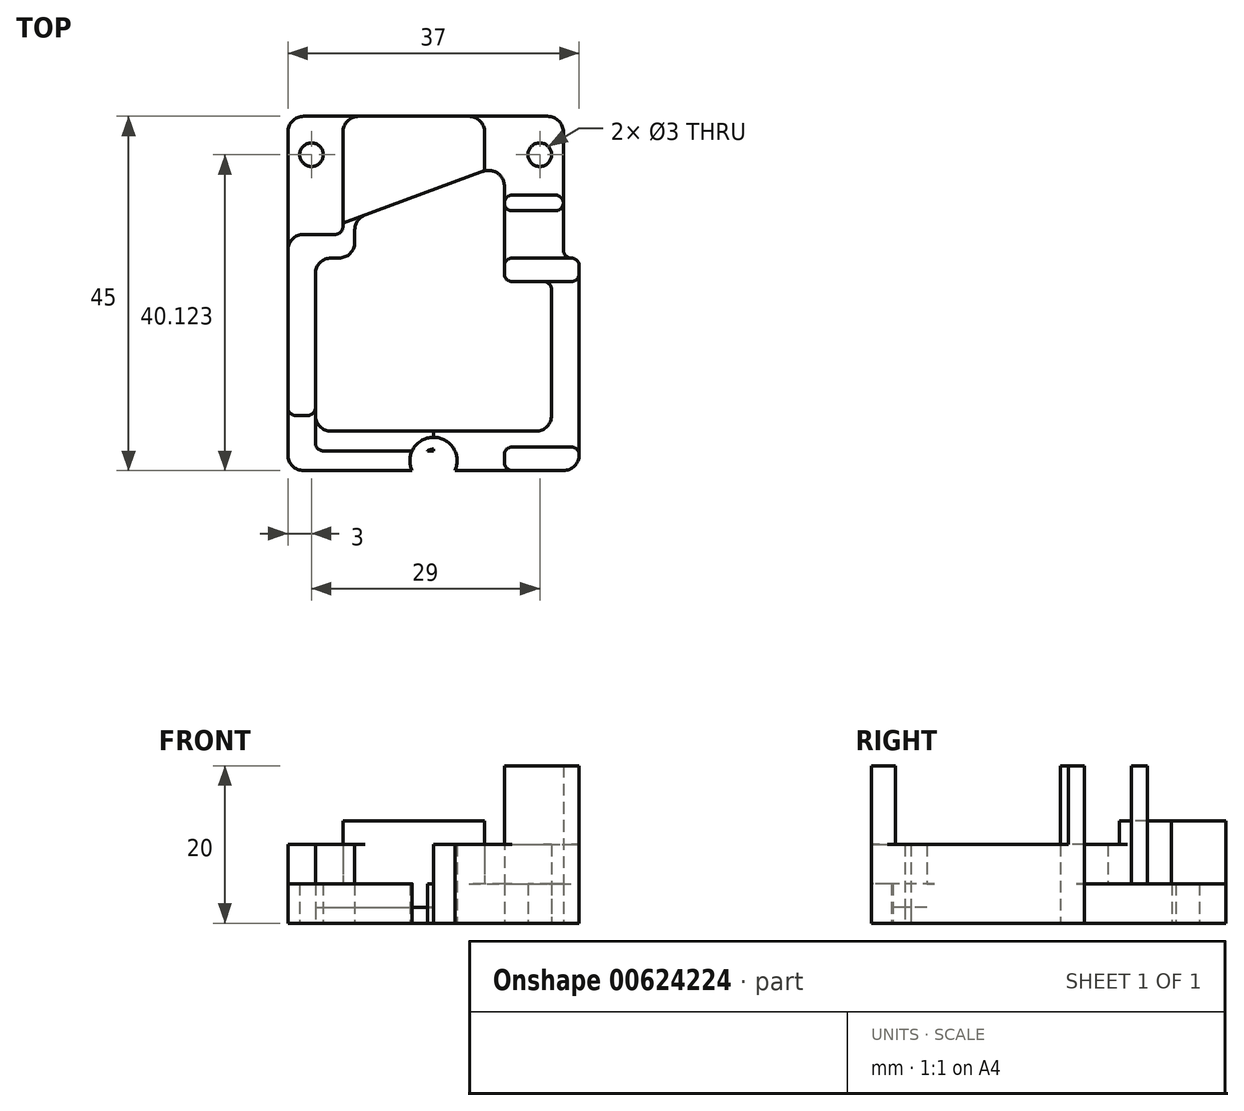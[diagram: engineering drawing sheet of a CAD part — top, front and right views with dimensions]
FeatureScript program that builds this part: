
annotation { "Feature Type Name" : "Feature", "Feature Type Description" : "" }
export const myFeature = defineFeature(function(context is Context, id is Id, definition is map)
    precondition{}
    {
        {
            var Q0;
            Q0=qCreatedBy(makeId("Top.planeOp"),FACE);
            var sketch = newSketch(context, id + "F0", { "sketchPlane" : qUnion([Q0])});
            skLineSegment(sketch, "E0.bottom", {"start": v(-16.5, 22.5) * mm, "end": v(14.5, 22.5) * mm});
            skLineSegment(sketch, "E0.top", {"start": v(-16.5, -22.5) * mm, "end": v(16.5, -22.5) * mm});
            skLineSegment(sketch, "E0.left", {"start": v(-18.5, 20.5) * mm, "end": v(-18.5, -20.5) * mm});
            skLineSegment(sketch, "E0.right", {"start": v(18.5, 3.5) * mm, "end": v(18.5, -20.5) * mm});
            skPoint(sketch, "E0.middle", {"position": v(0, 0) * mm});
            skLineSegment(sketch, "E1", {"start": v(-15, 2.5) * mm, "end": v(-15, -15.5) * mm});
            skLineSegment(sketch, "E2", {"start": v(-13, -17.5) * mm, "end": v(13, -17.5) * mm});
            skLineSegment(sketch, "E3", {"start": v(15, -15.5) * mm, "end": v(15, 0.5) * mm});
            skLineSegment(sketch, "E4", {"start": v(-13, 4.5) * mm, "end": v(-12, 4.5) * mm});
            skLineSegment(sketch, "E5", {"start": v(-10, 6.5) * mm, "end": v(-10, 8.1) * mm});
            skLineSegment(sketch, "E6", {"start": v(10, 1.5) * mm, "end": v(14, 1.5) * mm});
            skLineSegment(sketch, "E7", {"start": v(9, 2.5) * mm, "end": v(9, 13.63) * mm});
            skLineSegment(sketch, "E8", {"start": v(6.3, 15.5) * mm, "end": v(-8.7, 9.98) * mm});
            skLineSegment(sketch, "E9", {"start": v(16.5, 20.5) * mm, "end": v(16.5, 5.5) * mm});
            skLineSegment(sketch, "E10", {"start": v(17.5, 4.5) * mm, "end": v(17.5, 4.5) * mm});
            skPoint(sketch, "E11.visualSharp", {"position": v(-15, -17.5) * mm});
            skArc(sketch, "E11.filletArc", {"start": v(-15, -15.5) * mm, "mid": v(-14.41, -16.91) * mm, "end": v(-13, -17.5) * mm});
            skPoint(sketch, "E12.visualSharp", {"position": v(15, -17.5) * mm});
            skArc(sketch, "E12.filletArc", {"start": v(13, -17.5) * mm, "mid": v(14.41, -16.91) * mm, "end": v(15, -15.5) * mm});
            skPoint(sketch, "E13.visualSharp", {"position": v(-10, 4.5) * mm});
            skArc(sketch, "E13.filletArc", {"start": v(-12, 4.5) * mm, "mid": v(-10.59, 5.09) * mm, "end": v(-10, 6.5) * mm});
            skPoint(sketch, "E14.visualSharp", {"position": v(9, 16.5) * mm});
            skArc(sketch, "E14.filletArc", {"start": v(9, 13.63) * mm, "mid": v(8.14, 15.27) * mm, "end": v(6.3, 15.5) * mm});
            skPoint(sketch, "E15.visualSharp", {"position": v(-15, 4.5) * mm});
            skArc(sketch, "E15.filletArc", {"start": v(-13, 4.5) * mm, "mid": v(-14.41, 3.91) * mm, "end": v(-15, 2.5) * mm});
            skPoint(sketch, "E16.visualSharp", {"position": v(-10, 9.5) * mm});
            skArc(sketch, "E16.filletArc", {"start": v(-8.7, 9.98) * mm, "mid": v(-9.64, 9.25) * mm, "end": v(-10, 8.1) * mm});
            skPoint(sketch, "E17.visualSharp", {"position": v(-18.5, 22.5) * mm});
            skArc(sketch, "E17.filletArc", {"start": v(-16.5, 22.5) * mm, "mid": v(-17.91, 21.91) * mm, "end": v(-18.5, 20.5) * mm});
            skPoint(sketch, "E18.visualSharp", {"position": v(16.5, 22.5) * mm});
            skArc(sketch, "E18.filletArc", {"start": v(16.5, 20.5) * mm, "mid": v(15.91, 21.91) * mm, "end": v(14.5, 22.5) * mm});
            skPoint(sketch, "E19.visualSharp", {"position": v(18.5, -22.5) * mm});
            skArc(sketch, "E19.filletArc", {"start": v(16.5, -22.5) * mm, "mid": v(17.91, -21.91) * mm, "end": v(18.5, -20.5) * mm});
            skPoint(sketch, "E20.visualSharp", {"position": v(-18.5, -22.5) * mm});
            skArc(sketch, "E20.filletArc", {"start": v(-18.5, -20.5) * mm, "mid": v(-17.91, -21.91) * mm, "end": v(-16.5, -22.5) * mm});
            skPoint(sketch, "E21.visualSharp", {"position": v(9, 1.5) * mm});
            skArc(sketch, "E21.filletArc", {"start": v(9, 2.5) * mm, "mid": v(9.3, 1.8) * mm, "end": v(10, 1.5) * mm});
            skPoint(sketch, "E22.visualSharp", {"position": v(15, 1.5) * mm});
            skArc(sketch, "E22.filletArc", {"start": v(15, 0.5) * mm, "mid": v(14.7, 1.2) * mm, "end": v(14, 1.5) * mm});
            skPoint(sketch, "E23.visualSharp", {"position": v(16.5, 4.5) * mm});
            skArc(sketch, "E23.filletArc", {"start": v(16.5, 5.5) * mm, "mid": v(16.8, 4.8) * mm, "end": v(17.5, 4.5) * mm});
            skPoint(sketch, "E24.visualSharp", {"position": v(18.5, 4.5) * mm});
            skArc(sketch, "E24.filletArc", {"start": v(18.5, 3.5) * mm, "mid": v(18.2, 4.2) * mm, "end": v(17.5, 4.5) * mm});
            skLineSegment(sketch, "E25", {"start": v(-14, -20) * mm, "end": v(14, -20) * mm});
            skLineSegment(sketch, "E26", {"start": v(-15, -15.5) * mm, "end": v(-15, -19) * mm});
            skLineSegment(sketch, "E27", {"start": v(15, -15.5) * mm, "end": v(15, -19) * mm});
            skPoint(sketch, "E28.visualSharp", {"position": v(-15, -20) * mm});
            skArc(sketch, "E28.filletArc", {"start": v(-15, -19) * mm, "mid": v(-14.7, -19.7) * mm, "end": v(-14, -20) * mm});
            skPoint(sketch, "E29.visualSharp", {"position": v(15, -20) * mm});
            skArc(sketch, "E29.filletArc", {"start": v(14, -20) * mm, "mid": v(14.7, -19.7) * mm, "end": v(15, -19) * mm});
            skLineSegment(sketch, "E30", {"start": v(0, -17.5) * mm, "end": v(0, -23.8) * mm});
            skPoint(sketch, "E30.endSnap0", {"position": v(0, -22.5) * mm});
            skCircle(sketch, "E31", {"center": v(0, -21.28) * mm, "radius": 3 * mm});
            skCircle(sketch, "E32", {"center": v(0, -21.28) * mm, "radius": 1.5 * mm});
            skCircle(sketch, "E33", {"center": v(-15.5, 17.62) * mm, "radius": 3 * mm});
            skCircle(sketch, "E34", {"center": v(-15.5, 17.62) * mm, "radius": 1.5 * mm});
            skLineSegment(sketch, "E35", {"start": v(-15.5, 17.62) * mm, "end": v(14.6, 17.62) * mm, "construction": true});
            skCircle(sketch, "E36", {"center": v(13.5, 17.62) * mm, "radius": 3 * mm});
            skCircle(sketch, "E37", {"center": v(13.5, 17.62) * mm, "radius": 1.5 * mm});
            skSolve(sketch);
        }
        {
            var Q0;
            Q0=makeQuery(id+"F0.imprint","IMPRINT",FACE,{"disambiguationData":[TD([[makeQuery(id+"F0.imprint","IMPRINT",EDGE,{"derivedFrom":sQuery(id+"F0.wireOp",EDGE,"E0.bottom")}),-1.0]])]});
            var Q1;
            {var subQ0=sQuery(id+"F0.wireOp",EDGE,"E32");var subQ1=sQuery(id+"F0.wireOp",EDGE,"E25");var subQ2=makeQuery(id+"F0.imprint","INTERSECT",VERTEX,{"disambiguationData":[OD(1.0)],"derivedFrom":[subQ1,subQ0]});Q1=makeQuery(id+"F0.imprint","IMPRINT",FACE,{"disambiguationData":[TD([[makeQuery(id+"F0.imprint","IMPRINT",EDGE,{"disambiguationData":[TD([[subQ2,-1.0]])],"derivedFrom":subQ1}),1.0]])]});}
            var Q2;
            {var subQ0=sQuery(id+"F0.wireOp",EDGE,"E31");var subQ1=sQuery(id+"F0.wireOp",EDGE,"E25");var subQ2=makeQuery(id+"F0.imprint","INTERSECT",VERTEX,{"disambiguationData":[OD(0.0)],"derivedFrom":[subQ1,subQ0]});Q2=makeQuery(id+"F0.imprint","IMPRINT",FACE,{"disambiguationData":[TD([[makeQuery(id+"F0.imprint","IMPRINT",EDGE,{"disambiguationData":[TD([[subQ2,-1.0]])],"derivedFrom":subQ1}),1.0]])]});}
            var Q3;
            {var subQ0=sQuery(id+"F0.wireOp",EDGE,"E31");var subQ1=sQuery(id+"F0.wireOp",EDGE,"E0.top");var subQ2=makeQuery(id+"F0.imprint","INTERSECT",VERTEX,{"disambiguationData":[OD(1.0)],"derivedFrom":[subQ1,subQ0]});Q3=makeQuery(id+"F0.imprint","IMPRINT",FACE,{"disambiguationData":[TD([[makeQuery(id+"F0.imprint","IMPRINT",EDGE,{"disambiguationData":[TD([[subQ2,1.0]])],"derivedFrom":subQ1}),1.0]])]});}
            var Q4;
            {var subQ0=sQuery(id+"F0.wireOp",EDGE,"E31");var subQ1=sQuery(id+"F0.wireOp",EDGE,"E0.top");var subQ2=makeQuery(id+"F0.imprint","INTERSECT",VERTEX,{"disambiguationData":[OD(0.0)],"derivedFrom":[subQ1,subQ0]});Q4=makeQuery(id+"F0.imprint","IMPRINT",FACE,{"disambiguationData":[TD([[makeQuery(id+"F0.imprint","IMPRINT",EDGE,{"disambiguationData":[TD([[subQ2,-1.0]])],"derivedFrom":subQ1}),1.0]])]});}
            var Q5;
            {var subQ2=sQuery(id+"F0.wireOp",EDGE,"E0.top");var subQ4=sQuery(id+"F0.wireOp",EDGE,"E31");var subQ5=makeQuery(id+"F0.imprint","INTERSECT",VERTEX,{"disambiguationData":[OD(0.0)],"derivedFrom":[subQ2,subQ4]});Q5=makeQuery(id+"F0.imprint","IMPRINT",FACE,{"disambiguationData":[TD([[makeQuery(id+"F0.imprint","IMPRINT",EDGE,{"disambiguationData":[TD([[subQ5,-1.0]])],"derivedFrom":subQ2}),-1.0]])]});}
            var Q6;
            Q6=makeQuery(id+"F0.imprint","IMPRINT",FACE,{"disambiguationData":[TD([[makeQuery(id+"F0.imprint","IMPRINT",EDGE,{"derivedFrom":sQuery(id+"F0.wireOp",EDGE,"E33")}),1.0]])]});
            var Q7;
            Q7=makeQuery(id+"F0.imprint","IMPRINT",FACE,{"disambiguationData":[TD([[makeQuery(id+"F0.imprint","IMPRINT",EDGE,{"derivedFrom":sQuery(id+"F0.wireOp",EDGE,"E36")}),1.0]])]});
            extrude(context, id + "F1", {"entities" : qUnion([Q0, Q1, Q2, Q3, Q4, Q5, Q6, Q7]), "depth" : 5 * mm, "offsetDistance" : 25 * mm});
        }
        {
            var Q0;
            {var subQ4=sQuery(id+"F0.wireOp",EDGE,"E11.filletArc");Q0=makeQuery(id+"F0.imprint","IMPRINT",FACE,{"disambiguationData":[TD([[makeQuery(id+"F0.imprint","IMPRINT",EDGE,{"derivedFrom":subQ4}),-1.0]])]});}
            var Q1;
            {var subQ4=sQuery(id+"F0.wireOp",EDGE,"E12.filletArc");Q1=makeQuery(id+"F0.imprint","IMPRINT",FACE,{"disambiguationData":[TD([[makeQuery(id+"F0.imprint","IMPRINT",EDGE,{"derivedFrom":subQ4}),-1.0]])]});}
            extrude(context, id + "F2", {"entities" : qUnion([Q0, Q1]), "operationType" : NewBodyOperationType.ADD, "depth" : 2 * mm, "offsetDistance" : 25 * mm});
        }
        {
            var Q0;
            Q0=makeQuery(id+"F1.opExtrude","CAP_FACE",FACE,{"disambiguationData":[OSD([sQuery(id+"F0.wireOp",EDGE,"E0.bottom"),sQuery(id+"F0.wireOp",EDGE,"E0.top"),sQuery(id+"F0.wireOp",EDGE,"E0.left"),sQuery(id+"F0.wireOp",EDGE,"E0.right"),sQuery(id+"F0.wireOp",EDGE,"E1"),sQuery(id+"F0.wireOp",EDGE,"E3"),sQuery(id+"F0.wireOp",EDGE,"E4"),sQuery(id+"F0.wireOp",EDGE,"E5"),sQuery(id+"F0.wireOp",EDGE,"E6"),sQuery(id+"F0.wireOp",EDGE,"E7"),sQuery(id+"F0.wireOp",EDGE,"E8"),sQuery(id+"F0.wireOp",EDGE,"E9"),sQuery(id+"F0.wireOp",EDGE,"E13.filletArc"),sQuery(id+"F0.wireOp",EDGE,"E14.filletArc"),sQuery(id+"F0.wireOp",EDGE,"E15.filletArc"),sQuery(id+"F0.wireOp",EDGE,"E16.filletArc"),sQuery(id+"F0.wireOp",EDGE,"E17.filletArc"),sQuery(id+"F0.wireOp",EDGE,"E18.filletArc"),sQuery(id+"F0.wireOp",EDGE,"E19.filletArc"),sQuery(id+"F0.wireOp",EDGE,"E20.filletArc"),sQuery(id+"F0.wireOp",EDGE,"E21.filletArc"),sQuery(id+"F0.wireOp",EDGE,"E22.filletArc"),sQuery(id+"F0.wireOp",EDGE,"E23.filletArc"),sQuery(id+"F0.wireOp",EDGE,"E24.filletArc"),sQuery(id+"F0.wireOp",EDGE,"E25"),sQuery(id+"F0.wireOp",EDGE,"E26"),sQuery(id+"F0.wireOp",EDGE,"E27"),sQuery(id+"F0.wireOp",EDGE,"E28.filletArc"),sQuery(id+"F0.wireOp",EDGE,"E29.filletArc"),sQuery(id+"F0.wireOp",EDGE,"E31"),sQuery(id+"F0.wireOp",EDGE,"E32"),sQuery(id+"F0.wireOp",EDGE,"E34"),sQuery(id+"F0.wireOp",EDGE,"E37")])],"isStart":false});
            var sketch = newSketch(context, id + "F3", { "sketchPlane" : qUnion([Q0])});
            skLineSegment(sketch, "E38", {"start": v(-17.5, -15.5) * mm, "end": v(-16, -15.5) * mm});
            skLineSegment(sketch, "E39", {"start": v(-16.5, 7.5) * mm, "end": v(-12.5, 7.5) * mm});
            skLineSegment(sketch, "E40", {"start": v(-11.5, 8.5) * mm, "end": v(-11.5, 20.5) * mm});
            skLineSegment(sketch, "E41", {"start": v(6.5, 15.58) * mm, "end": v(6.5, 20.5) * mm});
            skLineSegment(sketch, "E42", {"start": v(-9.5, 22.5) * mm, "end": v(4.5, 22.5) * mm});
            skLineSegment(sketch, "E43", {"start": v(6.3, 15.5) * mm, "end": v(-11.5, 8.95) * mm});
            skLineSegment(sketch, "E44", {"start": v(-15, -14.5) * mm, "end": v(-15, 2.5) * mm});
            skPoint(sketch, "E45.visualSharp", {"position": v(-11.5, 22.5) * mm});
            skArc(sketch, "E45.filletArc", {"start": v(-9.5, 22.5) * mm, "mid": v(-10.91, 21.91) * mm, "end": v(-11.5, 20.5) * mm});
            skPoint(sketch, "E46.visualSharp", {"position": v(6.5, 22.5) * mm});
            skArc(sketch, "E46.filletArc", {"start": v(6.5, 20.5) * mm, "mid": v(5.91, 21.91) * mm, "end": v(4.5, 22.5) * mm});
            skLineSegment(sketch, "E47", {"start": v(-18.5, -14.5) * mm, "end": v(-18.5, 5.5) * mm});
            skPoint(sketch, "E48.visualSharp", {"position": v(-18.5, 7.5) * mm});
            skArc(sketch, "E48.filletArc", {"start": v(-16.5, 7.5) * mm, "mid": v(-17.91, 6.91) * mm, "end": v(-18.5, 5.5) * mm});
            skPoint(sketch, "E49.visualSharp", {"position": v(-18.5, -15.5) * mm});
            skArc(sketch, "E49.filletArc", {"start": v(-18.5, -14.5) * mm, "mid": v(-18.2, -15.2) * mm, "end": v(-17.5, -15.5) * mm});
            skPoint(sketch, "E50.visualSharp", {"position": v(-15, -15.5) * mm});
            skArc(sketch, "E50.filletArc", {"start": v(-16, -15.5) * mm, "mid": v(-15.3, -15.2) * mm, "end": v(-15, -14.5) * mm});
            skPoint(sketch, "E51.visualSharp", {"position": v(-11.5, 7.5) * mm});
            skArc(sketch, "E51.filletArc", {"start": v(-12.5, 7.5) * mm, "mid": v(-11.8, 7.8) * mm, "end": v(-11.5, 8.5) * mm});
            skLineSegment(sketch, "E52", {"start": v(6.3, 15.5) * mm, "end": v(6.5, 15.58) * mm});
            skLineSegment(sketch, "E53.bottom", {"start": v(10, 12.5) * mm, "end": v(15.5, 12.5) * mm});
            skLineSegment(sketch, "E53.top", {"start": v(10, 10.5) * mm, "end": v(15.5, 10.5) * mm});
            skLineSegment(sketch, "E53.left", {"start": v(9, 11.5) * mm, "end": v(9, 11.5) * mm});
            skLineSegment(sketch, "E53.right", {"start": v(16.5, 11.5) * mm, "end": v(16.5, 11.5) * mm});
            skLineSegment(sketch, "E54.bottom", {"start": v(10, 1.5) * mm, "end": v(17.5, 1.5) * mm});
            skLineSegment(sketch, "E54.top", {"start": v(10, 4.5) * mm, "end": v(17.5, 4.5) * mm});
            skLineSegment(sketch, "E54.left", {"start": v(9, 2.5) * mm, "end": v(9, 3.5) * mm});
            skLineSegment(sketch, "E54.right", {"start": v(18.5, 2.5) * mm, "end": v(18.5, 3.5) * mm});
            skLineSegment(sketch, "E55.bottom", {"start": v(10, -22.5) * mm, "end": v(16.5, -22.5) * mm});
            skLineSegment(sketch, "E55.top", {"start": v(10, -19.5) * mm, "end": v(17.5, -19.5) * mm});
            skLineSegment(sketch, "E55.left", {"start": v(9, -21.5) * mm, "end": v(9, -20.5) * mm});
            skLineSegment(sketch, "E55.right", {"start": v(18.5, -20.5) * mm, "end": v(18.5, -20.5) * mm});
            skLineSegment(sketch, "E56.bottom", {"start": v(13.25, 4.5) * mm, "end": v(12.25, 4.5) * mm});
            skLineSegment(sketch, "E56.left", {"start": v(13.25, 4.5) * mm, "end": v(13.25, 10.5) * mm});
            skLineSegment(sketch, "E56.right", {"start": v(12.25, 4.5) * mm, "end": v(12.25, 10.5) * mm});
            skPoint(sketch, "E56.middle", {"position": v(12.75, 10.5) * mm});
            skPoint(sketch, "E57.visualSharp", {"position": v(9, 12.5) * mm});
            skArc(sketch, "E57.filletArc", {"start": v(10, 12.5) * mm, "mid": v(9.3, 12.2) * mm, "end": v(9, 11.5) * mm});
            skPoint(sketch, "E58.visualSharp", {"position": v(16.5, 12.5) * mm});
            skArc(sketch, "E58.filletArc", {"start": v(16.5, 11.5) * mm, "mid": v(16.2, 12.2) * mm, "end": v(15.5, 12.5) * mm});
            skPoint(sketch, "E59.visualSharp", {"position": v(16.5, 10.5) * mm});
            skArc(sketch, "E59.filletArc", {"start": v(15.5, 10.5) * mm, "mid": v(16.2, 10.8) * mm, "end": v(16.5, 11.5) * mm});
            skPoint(sketch, "E60.visualSharp", {"position": v(9, 10.5) * mm});
            skArc(sketch, "E60.filletArc", {"start": v(9, 11.5) * mm, "mid": v(9.3, 10.8) * mm, "end": v(10, 10.5) * mm});
            skPoint(sketch, "E61.visualSharp", {"position": v(9, 4.5) * mm});
            skArc(sketch, "E61.filletArc", {"start": v(10, 4.5) * mm, "mid": v(9.3, 4.2) * mm, "end": v(9, 3.5) * mm});
            skPoint(sketch, "E62.visualSharp", {"position": v(9, 1.5) * mm});
            skArc(sketch, "E62.filletArc", {"start": v(9, 2.5) * mm, "mid": v(9.3, 1.8) * mm, "end": v(10, 1.5) * mm});
            skPoint(sketch, "E63.visualSharp", {"position": v(18.5, 1.5) * mm});
            skArc(sketch, "E63.filletArc", {"start": v(17.5, 1.5) * mm, "mid": v(18.2, 1.8) * mm, "end": v(18.5, 2.5) * mm});
            skPoint(sketch, "E64.visualSharp", {"position": v(18.5, 4.5) * mm});
            skArc(sketch, "E64.filletArc", {"start": v(18.5, 3.5) * mm, "mid": v(18.2, 4.2) * mm, "end": v(17.5, 4.5) * mm});
            skPoint(sketch, "E65.visualSharp", {"position": v(9, -19.5) * mm});
            skArc(sketch, "E65.filletArc", {"start": v(10, -19.5) * mm, "mid": v(9.3, -19.8) * mm, "end": v(9, -20.5) * mm});
            skPoint(sketch, "E66.visualSharp", {"position": v(9, -22.5) * mm});
            skArc(sketch, "E66.filletArc", {"start": v(9, -21.5) * mm, "mid": v(9.3, -22.2) * mm, "end": v(10, -22.5) * mm});
            skPoint(sketch, "E67.visualSharp", {"position": v(18.5, -19.5) * mm});
            skArc(sketch, "E67.filletArc", {"start": v(18.5, -20.5) * mm, "mid": v(18.2, -19.8) * mm, "end": v(17.5, -19.5) * mm});
            skPoint(sketch, "E68.visualSharp", {"position": v(18.5, -22.5) * mm});
            skArc(sketch, "E68.filletArc", {"start": v(16.5, -22.5) * mm, "mid": v(17.91, -21.91) * mm, "end": v(18.5, -20.5) * mm});
            skSolve(sketch);
        }
        {
            var Q0;
            Q0=makeQuery(id+"F3.imprint","IMPRINT",FACE,{"disambiguationData":[TD([[makeQuery(id+"F3.imprint","IMPRINT",EDGE,{"derivedFrom":sQuery(id+"F3.wireOp",EDGE,"E38")}),1.0]])]});
            extrude(context, id + "F4", {"entities" : qUnion([Q0]), "operationType" : NewBodyOperationType.ADD, "depth" : 5 * mm, "offsetDistance" : 25 * mm});
        }
        {
            var Q0;
            Q0=makeQuery(id+"F3.imprint","IMPRINT",FACE,{"disambiguationData":[TD([[makeQuery(id+"F3.imprint","IMPRINT",EDGE,{"derivedFrom":sQuery(id+"F3.wireOp",EDGE,"E41")}),1.0]])]});
            extrude(context, id + "F5", {"entities" : qUnion([Q0]), "operationType" : NewBodyOperationType.ADD, "depth" : 8 * mm, "offsetDistance" : 25 * mm});
        }
        {
            var Q0;
            {var subQ0=sQuery(id+"F3.wireOp",EDGE,"E65.filletArc");var subQ1=sQuery(id+"F3.wireOp",EDGE,"E55.top");var subQ2=makeQuery(id+"F3.imprint","INTERSECT",VERTEX,{"derivedFrom":[subQ1,subQ0]});Q0=makeQuery(id+"F3.imprint","IMPRINT",FACE,{"disambiguationData":[TD([[makeQuery(id+"F3.imprint","IMPRINT",EDGE,{"disambiguationData":[TD([[subQ2,-1.0]])],"derivedFrom":subQ1}),-1.0]])]});}
            var Q1;
            Q1=makeQuery(id+"F3.imprint","IMPRINT",FACE,{"disambiguationData":[TD([[makeQuery(id+"F3.imprint","IMPRINT",EDGE,{"derivedFrom":sQuery(id+"F3.wireOp",EDGE,"E55.bottom")}),1.0]])]});
            extrude(context, id + "F6", {"entities" : qUnion([Q0, Q1]), "operationType" : NewBodyOperationType.ADD, "depth" : 15 * mm, "offsetDistance" : 25 * mm});
        }
        {
            var Q0;
            Q0=makeQuery(id+"F3.imprint","IMPRINT",FACE,{"disambiguationData":[TD([[makeQuery(id+"F3.imprint","IMPRINT",EDGE,{"derivedFrom":sQuery(id+"F3.wireOp",EDGE,"E53.bottom")}),-1.0]])]});
            var Q1;
            Q1=makeQuery(id+"F3.imprint","IMPRINT",FACE,{"disambiguationData":[TD([[makeQuery(id+"F3.imprint","IMPRINT",EDGE,{"derivedFrom":sQuery(id+"F3.wireOp",EDGE,"E54.left")}),-1.0]])]});
            extrude(context, id + "F7", {"entities" : qUnion([Q0, Q1]), "operationType" : NewBodyOperationType.ADD, "depth" : 15 * mm, "offsetDistance" : 25 * mm});
        }
        {
            var Q0;
            Q0=makeQuery(id+"F3.imprint","IMPRINT",FACE,{"disambiguationData":[TD([[makeQuery(id+"F3.imprint","IMPRINT",EDGE,{"derivedFrom":sQuery(id+"F3.wireOp",EDGE,"E56.bottom")}),-1.0]])]});
            var Q1;
            {var subQ0=sQuery(id+"F3.wireOp",EDGE,"E67.filletArc");Q1=makeQuery(id+"F3.imprint","IMPRINT",FACE,{"disambiguationData":[TD([[makeQuery(id+"F3.imprint","IMPRINT",EDGE,{"derivedFrom":subQ0}),-1.0]])]});}
            extrude(context, id + "F8", {"entities" : qUnion([Q0, Q1]), "operationType" : NewBodyOperationType.ADD, "depth" : 5 * mm, "offsetDistance" : 25 * mm});
        }
    });
